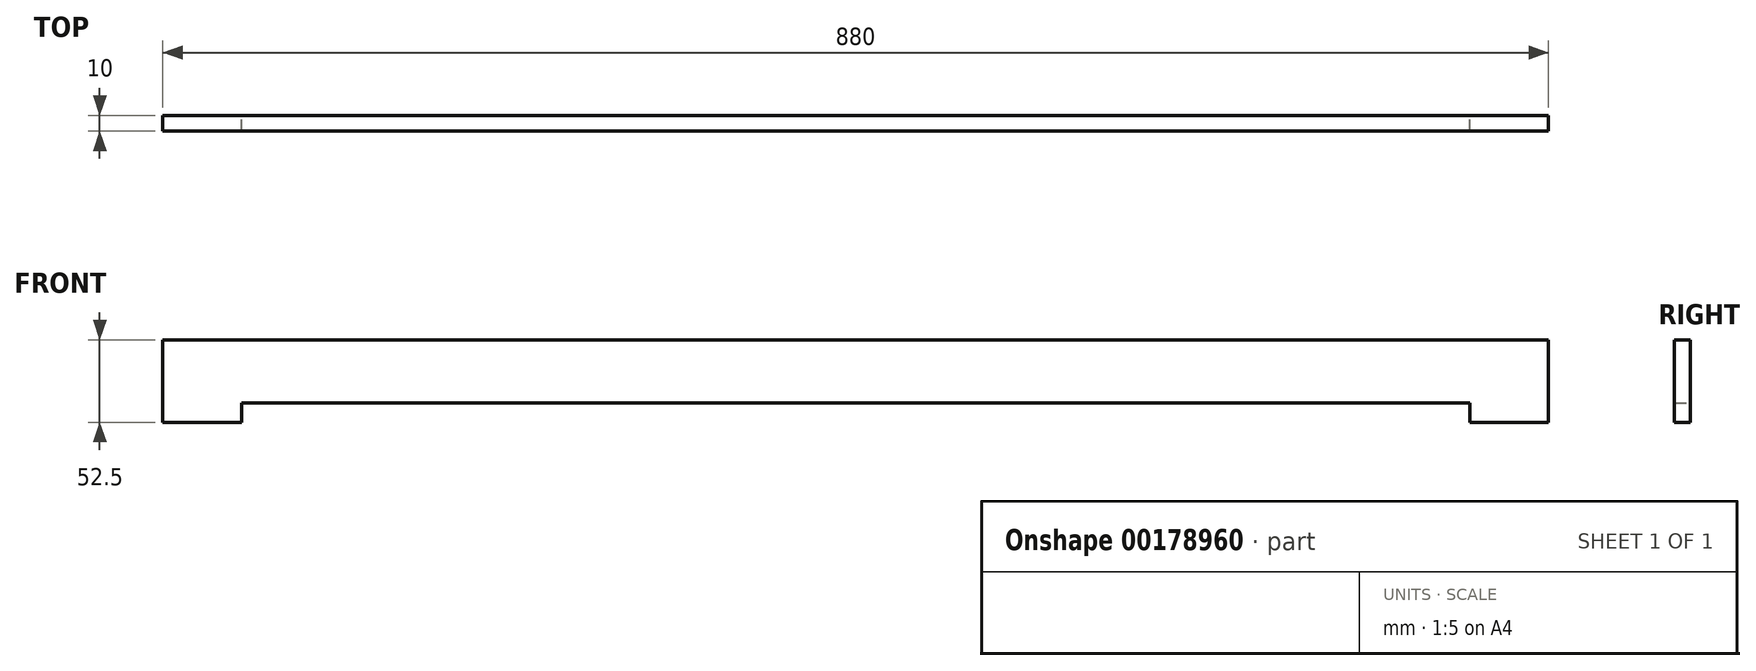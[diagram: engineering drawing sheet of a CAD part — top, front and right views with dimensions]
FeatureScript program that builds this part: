
annotation { "Feature Type Name" : "Feature", "Feature Type Description" : "" }
export const myFeature = defineFeature(function(context is Context, id is Id, definition is map)
    precondition{}
    {
        {
            var Q0;
            Q0=qCreatedBy(makeId("Front.planeOp"),FACE);
            var sketch = newSketch(context, id + "F0", { "sketchPlane" : qUnion([Q0])});
            skLineSegment(sketch, "E0.bottom", {"start": v(440, -80) * mm, "end": v(390, -80) * mm});
            skLineSegment(sketch, "E0.top", {"start": v(440, 80) * mm, "end": v(-440, 80) * mm});
            skLineSegment(sketch, "E0.left", {"start": v(440, -80) * mm, "end": v(440, 80) * mm});
            skLineSegment(sketch, "E0.right", {"start": v(-440, -80) * mm, "end": v(-440, 80) * mm});
            skPoint(sketch, "E0.middle", {"position": v(0, 0) * mm});
            skLineSegment(sketch, "E1", {"start": v(-390, -67.5) * mm, "end": v(-390, -80) * mm});
            skLineSegment(sketch, "E2", {"start": v(390, -67.5) * mm, "end": v(390, -80) * mm});
            skLineSegment(sketch, "E3", {"start": v(-390, -67.5) * mm, "end": v(390, -67.5) * mm});
            skLineSegment(sketch, "E4.trimOffspring", {"start": v(-390, -80) * mm, "end": v(-440, -80) * mm});
            skCircle(sketch, "E5", {"center": v(-369, 60) * mm, "radius": 4 * mm});
            skCircle(sketch, "E6", {"center": v(-369, 20) * mm, "radius": 4 * mm});
            skCircle(sketch, "E7", {"center": v(-329, 60) * mm, "radius": 3 * mm});
            skCircle(sketch, "E8", {"center": v(369, 60) * mm, "radius": 4 * mm});
            skCircle(sketch, "E9", {"center": v(369, 20) * mm, "radius": 4 * mm});
            skCircle(sketch, "E10", {"center": v(329, 60) * mm, "radius": 3 * mm});
            skLineSegment(sketch, "E11", {"start": v(-440, -27.5) * mm, "end": v(440, -27.5) * mm});
            skLineSegment(sketch, "E12", {"start": v(0, 80) * mm, "end": v(0, -27.5) * mm});
            skSolve(sketch);
        }
        {
            var Q0;
            Q0=makeQuery(id+"F0.imprint","IMPRINT",FACE,{"disambiguationData":[TD([[makeQuery(id+"F0.imprint","IMPRINT",EDGE,{"derivedFrom":sQuery(id+"F0.wireOp",EDGE,"E0.bottom")}),-1.0]])]});
            extrude(context, id + "F1", {"entities" : qUnion([Q0]), "depth" : 10 * mm});
        }
    });
